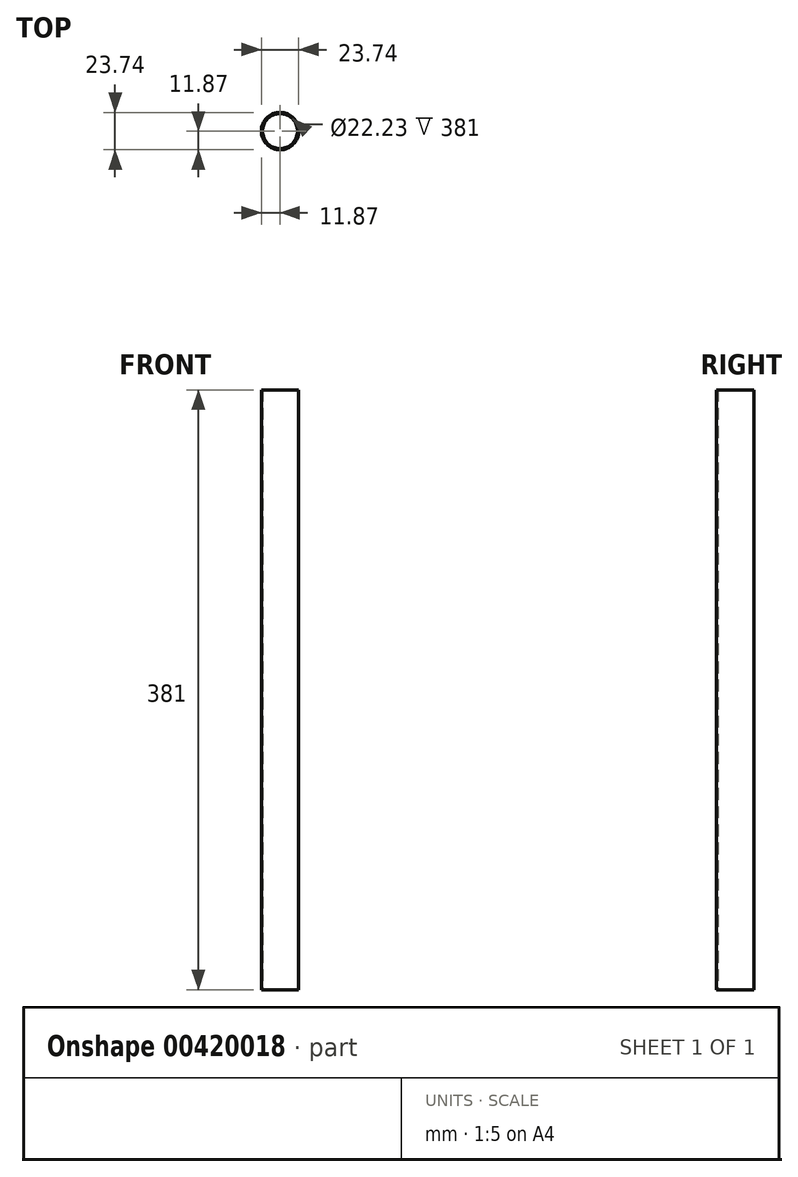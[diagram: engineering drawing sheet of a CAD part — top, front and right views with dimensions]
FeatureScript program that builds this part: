
annotation { "Feature Type Name" : "Feature", "Feature Type Description" : "" }
export const myFeature = defineFeature(function(context is Context, id is Id, definition is map)
    precondition{}
    {
        {
            var Q0;
            Q0=qCreatedBy(makeId("Top.planeOp"),FACE);
            var sketch = newSketch(context, id + "F0", { "sketchPlane" : qUnion([Q0])});
            skCircle(sketch, "E0", {"center": v(0, 0) * mm, "radius": 11.87 * mm});
            skCircle(sketch, "E1", {"center": v(0, 0) * mm, "radius": 11.11 * mm});
            skSolve(sketch);
        }
        {
            var Q0;
            Q0 = qSketchRegion(id + "F0", true);
            extrude(context, id + "F1", {"entities" : qUnion([Q0]), "depth" : 381 * mm});
        }
    });
